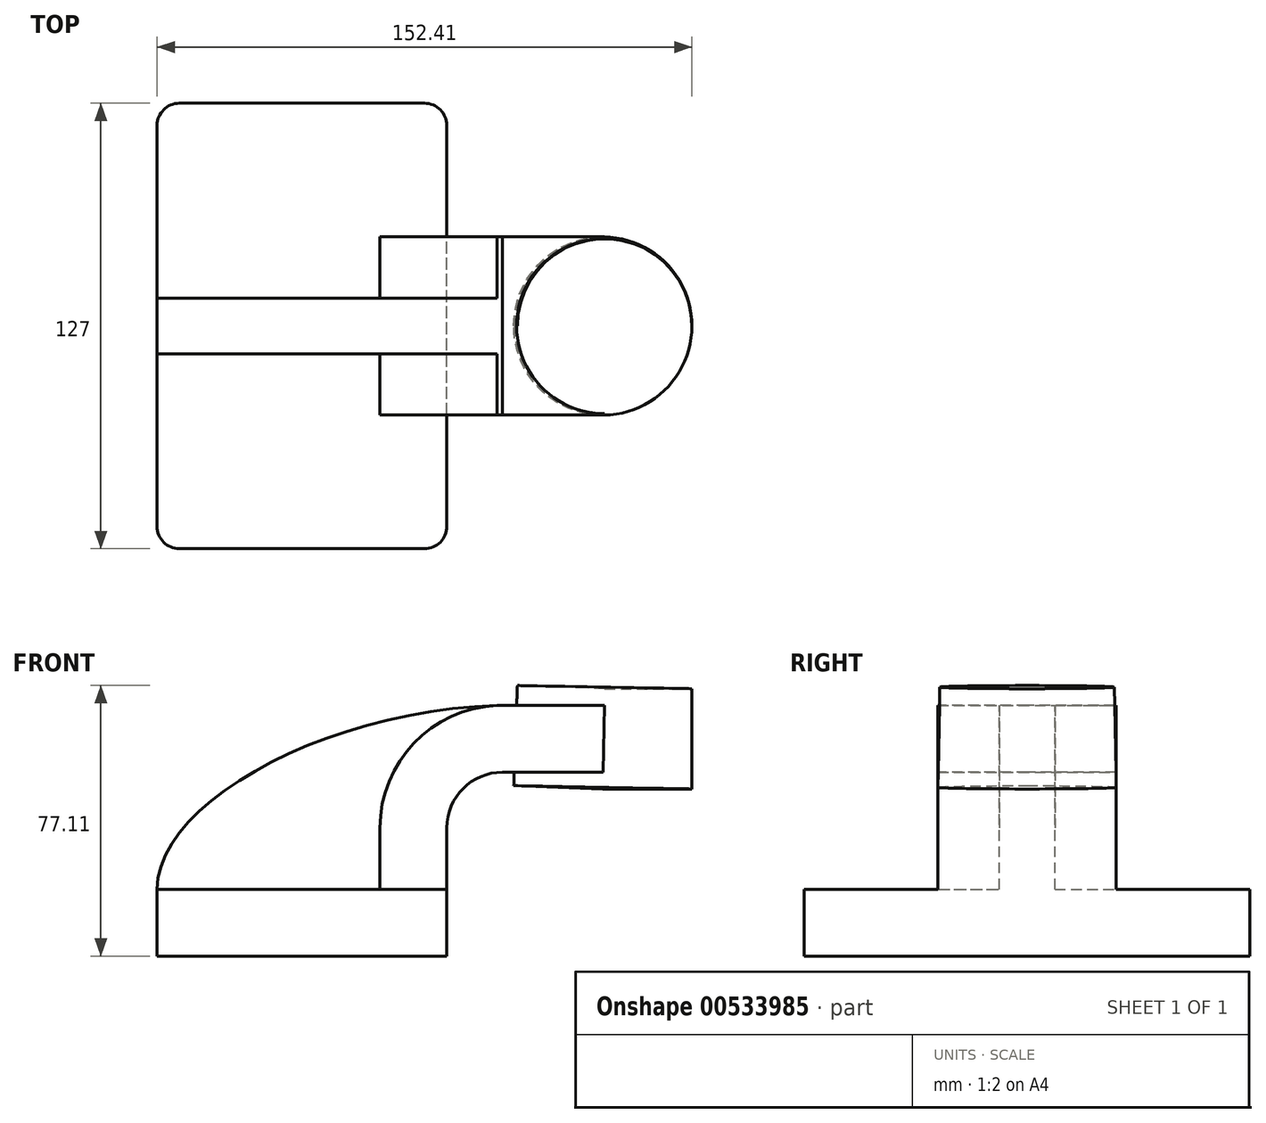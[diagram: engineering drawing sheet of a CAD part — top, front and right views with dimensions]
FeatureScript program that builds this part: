
annotation { "Feature Type Name" : "Feature", "Feature Type Description" : "" }
export const myFeature = defineFeature(function(context is Context, id is Id, definition is map)
    precondition{}
    {
        {
            var Q0;
            Q0=qCreatedBy(makeId("Front.planeOp"),FACE);
            var sketch = newSketch(context, id + "F0", { "sketchPlane" : qUnion([Q0])});
            skLineSegment(sketch, "E0.bottom", {"start": v(-41.28, -9.53) * mm, "end": v(41.28, -9.53) * mm});
            skLineSegment(sketch, "E0.top", {"start": v(-41.28, 9.52) * mm, "end": v(41.27, 9.52) * mm});
            skLineSegment(sketch, "E0.left", {"start": v(-41.27, -9.53) * mm, "end": v(-41.28, 9.52) * mm});
            skLineSegment(sketch, "E0.right", {"start": v(41.28, -9.53) * mm, "end": v(41.27, 9.52) * mm});
            skPoint(sketch, "E0.middle", {"position": v(0, 0) * mm});
            skLineSegment(sketch, "E1.bottom", {"start": v(60.32, 38.1) * mm, "end": v(111.12, 38.1) * mm});
            skLineSegment(sketch, "E1.top", {"start": v(60.32, 66.67) * mm, "end": v(111.12, 66.67) * mm});
            skLineSegment(sketch, "E1.left", {"start": v(60.32, 38.1) * mm, "end": v(60.32, 66.67) * mm});
            skLineSegment(sketch, "E1.right", {"start": v(111.12, 38.1) * mm, "end": v(111.12, 66.67) * mm});
            skPoint(sketch, "E1.middle", {"position": v(85.72, 52.39) * mm});
            skLineSegment(sketch, "E2", {"start": v(41.27, 9.52) * mm, "end": v(41.27, 27) * mm});
            skArc(sketch, "E3", {"start": v(41.27, 27) * mm, "mid": v(45.92, 38.23) * mm, "end": v(57.15, 42.88) * mm});
            skLineSegment(sketch, "E4", {"start": v(57.15, 42.88) * mm, "end": v(86.25, 42.88) * mm});
            skLineSegment(sketch, "E5.0", {"start": v(57.15, 61.93) * mm, "end": v(86.25, 61.93) * mm});
            skArc(sketch, "E5.1", {"start": v(22.22, 27) * mm, "mid": v(32.45, 51.7) * mm, "end": v(57.15, 61.93) * mm});
            skLineSegment(sketch, "E5.2", {"start": v(22.22, 9.52) * mm, "end": v(22.22, 27) * mm});
            skLineSegment(sketch, "E6", {"start": v(85.72, 38.1) * mm, "end": v(86.25, 66.67) * mm});
            skFitSpline(sketch, "E7", {"points": [v(-41.28, 9.52) * mm, v(57.15, 61.93) * mm], "startDerivative": vector(-0.06, 75.02) * mm, "endDerivative": vector(147.43, 2.49) * mm});
            skSolve(sketch);
        }
        {
            var Q0;
            Q0=makeQuery(id+"F0.imprint","IMPRINT",FACE,{"disambiguationData":[TD([[makeQuery(id+"F0.imprint","IMPRINT",EDGE,{"derivedFrom":sQuery(id+"F0.wireOp",EDGE,"E0.bottom")}),1.0]])]});
            extrude(context, id + "F1", {"entities" : qUnion([Q0]), "endBound" : BoundingType.SYMMETRIC, "depth" : 127 * mm, "offsetDistance" : 25.4 * mm});
        }
        {
            var Q0;
            {var subQ1=sQuery(id+"F0.wireOp",EDGE,"E2");Q0=makeQuery(id+"F0.imprint","IMPRINT",FACE,{"disambiguationData":[TD([[makeQuery(id+"F0.imprint","IMPRINT",EDGE,{"derivedFrom":subQ1}),1.0]])]});}
            var Q1;
            {var subQ0=sQuery(id+"F0.wireOp",EDGE,"E4");var subQ1=sQuery(id+"F0.wireOp",EDGE,"E1.left");var subQ2=makeQuery(id+"F0.imprint","INTERSECT",VERTEX,{"derivedFrom":[subQ1,subQ0]});Q1=makeQuery(id+"F0.imprint","IMPRINT",FACE,{"disambiguationData":[TD([[makeQuery(id+"F0.imprint","IMPRINT",EDGE,{"disambiguationData":[TD([[subQ2,-1.0]])],"derivedFrom":subQ1}),-1.0]])]});}
            extrude(context, id + "F2", {"entities" : qUnion([Q0, Q1]), "operationType" : NewBodyOperationType.ADD, "endBound" : BoundingType.SYMMETRIC, "depth" : 50.8 * mm, "offsetDistance" : 25.4 * mm});
        }
        {
            var Q0;
            {var subQ3=sQuery(id+"F0.wireOp",EDGE,"E5.2");Q0=makeQuery(id+"F0.imprint","IMPRINT",FACE,{"disambiguationData":[TD([[makeQuery(id+"F0.imprint","IMPRINT",EDGE,{"derivedFrom":subQ3}),1.0]])]});}
            extrude(context, id + "F3", {"entities" : qUnion([Q0]), "operationType" : NewBodyOperationType.ADD, "endBound" : BoundingType.SYMMETRIC, "depth" : 15.88 * mm, "offsetDistance" : 25.4 * mm});
        }
        {
            var Q0;
            {var subQ4=sQuery(id+"F0.wireOp",EDGE,"E1.right");Q0=makeQuery(id+"F0.imprint","IMPRINT",FACE,{"disambiguationData":[TD([[makeQuery(id+"F0.imprint","IMPRINT",EDGE,{"derivedFrom":subQ4}),1.0]])]});}
            var Q1;
            Q1=sQuery(id+"F0.wireOp",EDGE,"E6");
            revolve(context, id + "F4", {"operationType" : NewBodyOperationType.ADD, "entities" : qUnion([Q0]), "axis" : qUnion([Q1]), "revolveType" : RevolveType.FULL});
        }
        {
            var Q0;
            Q0=makeQuery(id+"F1.opExtrude","CAP_EDGE",EDGE,{"disambiguationData":[OSD([sQuery(id+"F0.wireOp",EDGE,"E0.left")])],"isStart":false});
            var Q1;
            Q1=makeQuery(id+"F1.opExtrude","CAP_EDGE",EDGE,{"disambiguationData":[OSD([sQuery(id+"F0.wireOp",EDGE,"E0.right")])],"isStart":false});
            var Q2;
            Q2=makeQuery(id+"F1.opExtrude","CAP_EDGE",EDGE,{"disambiguationData":[OSD([sQuery(id+"F0.wireOp",EDGE,"E0.right")])],"isStart":true});
            var Q3;
            Q3=makeQuery(id+"F1.opExtrude","CAP_EDGE",EDGE,{"disambiguationData":[OSD([sQuery(id+"F0.wireOp",EDGE,"E0.left")])],"isStart":true});
            fillet(context, id + "F5", {"entities" : qUnion([Q0, Q1, Q2, Q3]), "radius" : 6.35 * mm, "tangentPropagation" : true, "allowEdgeOverflow" : false});
        }
    });
